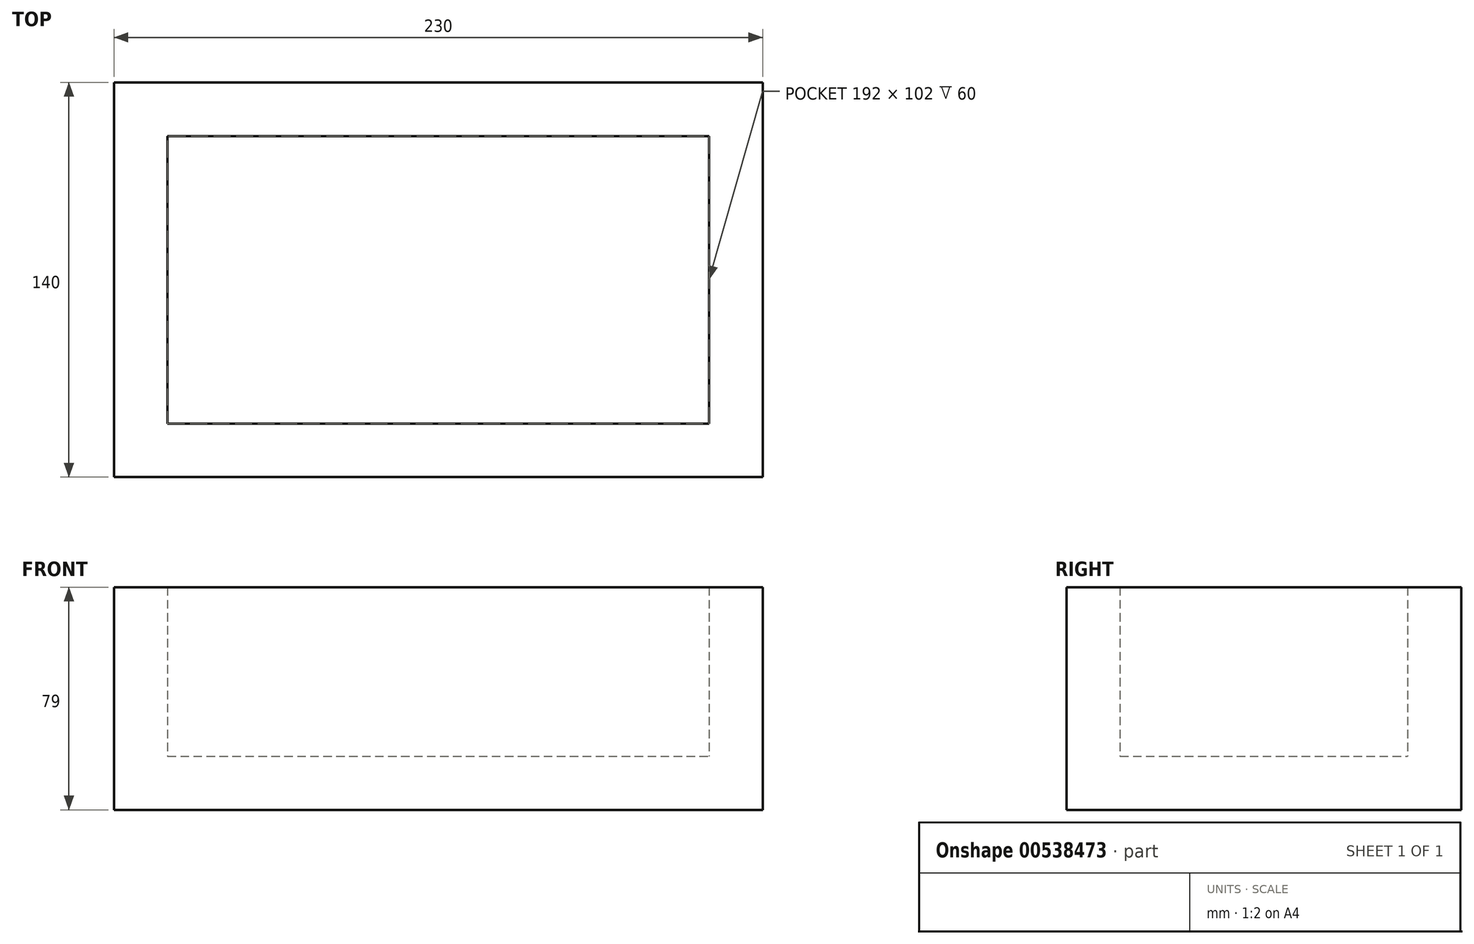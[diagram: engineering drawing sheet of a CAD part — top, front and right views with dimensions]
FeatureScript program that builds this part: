
annotation { "Feature Type Name" : "Feature", "Feature Type Description" : "" }
export const myFeature = defineFeature(function(context is Context, id is Id, definition is map)
    precondition{}
    {
        {
            var Q0;
            Q0=qCreatedBy(makeId("Top.planeOp"),FACE);
            var sketch = newSketch(context, id + "F0", { "sketchPlane" : qUnion([Q0])});
            skLineSegment(sketch, "E0.bottom", {"start": v(-115, 70) * mm, "end": v(115, 70) * mm});
            skLineSegment(sketch, "E0.top", {"start": v(-115, -70) * mm, "end": v(115, -70) * mm});
            skLineSegment(sketch, "E0.left", {"start": v(-115, 70) * mm, "end": v(-115, -70) * mm});
            skLineSegment(sketch, "E0.right", {"start": v(115, 70) * mm, "end": v(115, -70) * mm});
            skPoint(sketch, "E0.middle", {"position": v(0, 0) * mm});
            skSolve(sketch);
        }
        {
            var Q0;
            Q0 = qSketchRegion(id + "F0", true);
            extrude(context, id + "F1", {"entities" : qUnion([Q0]), "depth" : 19 * mm, "offsetDistance" : 25 * mm});
        }
        {
            var Q0;
            Q0=makeQuery(id+"F1.opExtrude","CAP_FACE",FACE,{"disambiguationData":[OSD([sQuery(id+"F0.wireOp",EDGE,"E0.bottom"),sQuery(id+"F0.wireOp",EDGE,"E0.top"),sQuery(id+"F0.wireOp",EDGE,"E0.left"),sQuery(id+"F0.wireOp",EDGE,"E0.right")])],"isStart":false});
            var sketch = newSketch(context, id + "F2", { "sketchPlane" : qUnion([Q0])});
            skLineSegment(sketch, "E1.bottom", {"start": v(-115, -70) * mm, "end": v(115, -70) * mm});
            skLineSegment(sketch, "E1.top", {"start": v(-115, 70) * mm, "end": v(115, 70) * mm});
            skLineSegment(sketch, "E1.left", {"start": v(-115, -70) * mm, "end": v(-115, 70) * mm});
            skLineSegment(sketch, "E1.right", {"start": v(115, -70) * mm, "end": v(115, 70) * mm});
            skLineSegment(sketch, "E2.bottom", {"start": v(-96, -51) * mm, "end": v(96, -51) * mm});
            skLineSegment(sketch, "E2.top", {"start": v(-96, 51) * mm, "end": v(96, 51) * mm});
            skLineSegment(sketch, "E2.left", {"start": v(-96, -51) * mm, "end": v(-96, 51) * mm});
            skLineSegment(sketch, "E2.right", {"start": v(96, -51) * mm, "end": v(96, 51) * mm});
            skSolve(sketch);
        }
        {
            var Q0;
            Q0=makeQuery(id+"F2.imprint","IMPRINT",FACE,{"disambiguationData":[TD([[makeQuery(id+"F2.imprint","IMPRINT",EDGE,{"derivedFrom":sQuery(id+"F2.wireOp",EDGE,"E1.bottom")}),1.0]])]});
            extrude(context, id + "F3", {"entities" : qUnion([Q0]), "operationType" : NewBodyOperationType.ADD, "depth" : 60 * mm, "offsetDistance" : 25 * mm});
        }
    });
